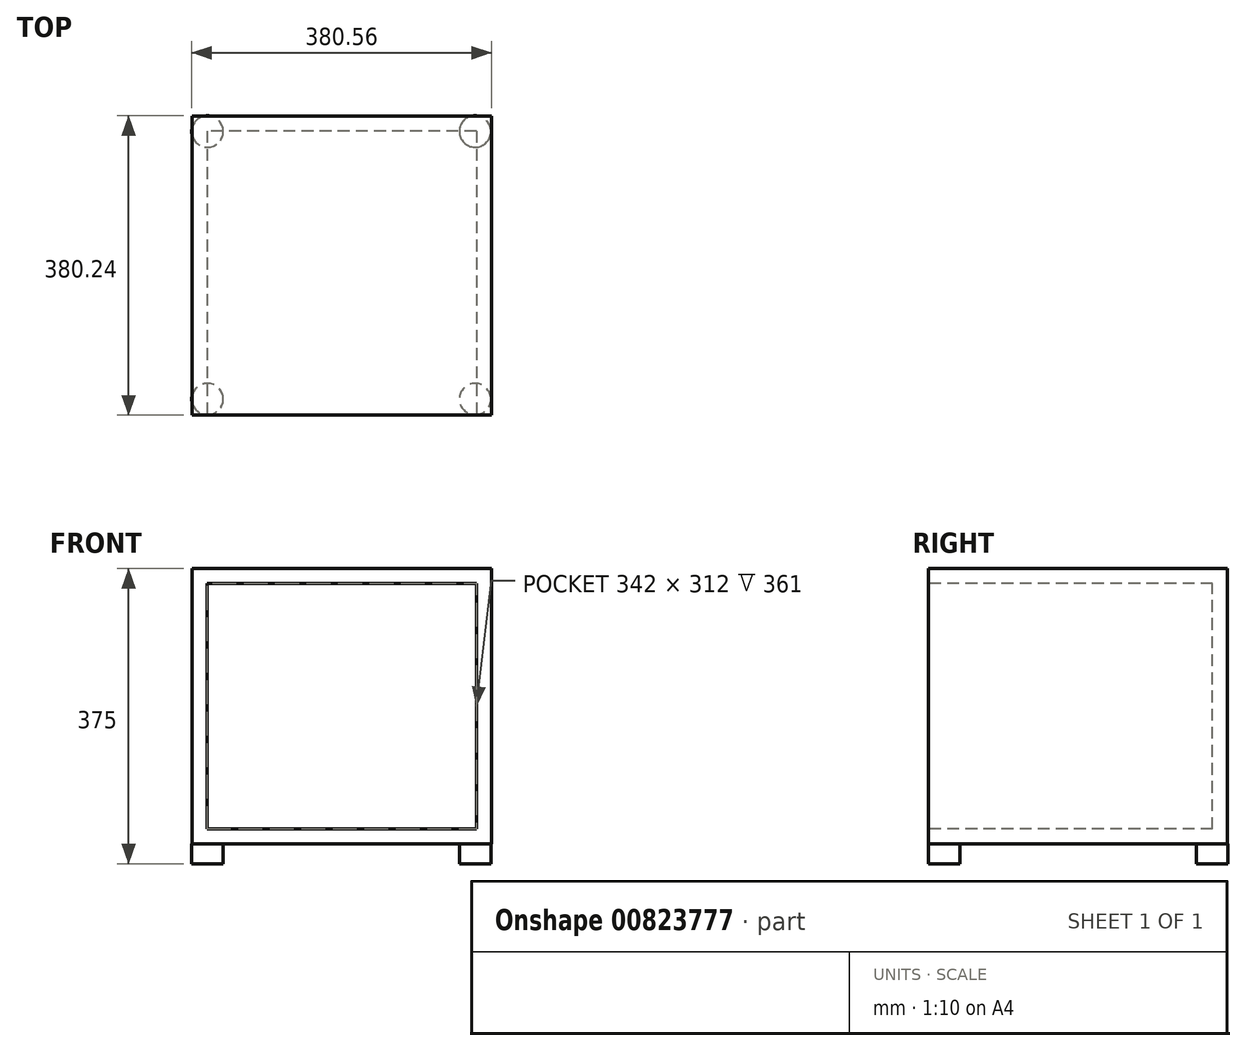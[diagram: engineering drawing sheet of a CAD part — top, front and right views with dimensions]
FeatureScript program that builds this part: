
annotation { "Feature Type Name" : "Feature", "Feature Type Description" : "" }
export const myFeature = defineFeature(function(context is Context, id is Id, definition is map)
    precondition{}
    {
        {
            var Q0;
            Q0=qCreatedBy(makeId("Top.planeOp"),FACE);
            var sketch = newSketch(context, id + "F0", { "sketchPlane" : qUnion([Q0])});
            skLineSegment(sketch, "E0.bottom", {"start": v(190, -190) * mm, "end": v(-190, -190) * mm});
            skLineSegment(sketch, "E0.top", {"start": v(190, 190) * mm, "end": v(-190, 190) * mm});
            skLineSegment(sketch, "E0.left", {"start": v(190, -190) * mm, "end": v(190, 190) * mm});
            skLineSegment(sketch, "E0.right", {"start": v(-190, -190) * mm, "end": v(-190, 190) * mm});
            skPoint(sketch, "E0.middle", {"position": v(0, 0) * mm});
            skSolve(sketch);
        }
        {
            var Q0;
            Q0=makeQuery(id+"F0.imprint","IMPRINT",FACE,{"disambiguationData":[TD([[makeQuery(id+"F0.imprint","IMPRINT",EDGE,{"derivedFrom":sQuery(id+"F0.wireOp",EDGE,"E0.bottom")}),-1.0]])]});
            extrude(context, id + "F1", {"entities" : qUnion([Q0]), "depth" : 350 * mm, "offsetDistance" : 25 * mm});
        }
        {
            var Q0;
            Q0=makeQuery(id+"F1.opExtrude","SWEPT_FACE",FACE,{"disambiguationData":[OSD([sQuery(id+"F0.wireOp",EDGE,"E0.bottom")])]});
            var sketch = newSketch(context, id + "F2", { "sketchPlane" : qUnion([Q0])});
            skLineSegment(sketch, "E1.bottom", {"start": v(171, 19) * mm, "end": v(-171, 19) * mm});
            skLineSegment(sketch, "E1.top", {"start": v(171, 331) * mm, "end": v(-171, 331) * mm});
            skLineSegment(sketch, "E1.left", {"start": v(171, 19) * mm, "end": v(171, 331) * mm});
            skLineSegment(sketch, "E1.right", {"start": v(-171, 19) * mm, "end": v(-171, 331) * mm});
            skPoint(sketch, "E1.middle", {"position": v(0, 175) * mm});
            skSolve(sketch);
        }
        {
            var Q0;
            Q0=makeQuery(id+"F2.imprint","IMPRINT",FACE,{"disambiguationData":[TD([[makeQuery(id+"F2.imprint","IMPRINT",EDGE,{"derivedFrom":sQuery(id+"F2.wireOp",EDGE,"E1.bottom")}),-1.0]])]});
            extrude(context, id + "F3", {"entities" : qUnion([Q0]), "operationType" : NewBodyOperationType.REMOVE, "oppositeDirection" : true, "depth" : 361 * mm, "offsetDistance" : 25 * mm});
        }
        {
            var Q0;
            Q0=makeQuery(id+"F0.imprint","IMPRINT",FACE,{"disambiguationData":[TD([[makeQuery(id+"F0.imprint","IMPRINT",EDGE,{"derivedFrom":sQuery(id+"F0.wireOp",EDGE,"E0.bottom")}),-1.0]])]});
            var sketch = newSketch(context, id + "F4", { "sketchPlane" : qUnion([Q0])});
            skCircle(sketch, "E2", {"center": v(169.44, -169.76) * mm, "radius": 20 * mm});
            skCircle(sketch, "E3", {"center": v(169.44, 170.24) * mm, "radius": 20 * mm});
            skCircle(sketch, "E4", {"center": v(-170.56, 170.24) * mm, "radius": 20 * mm});
            skCircle(sketch, "E5", {"center": v(-170.56, -169.76) * mm, "radius": 20 * mm});
            skSolve(sketch);
        }
        {
            var Q0;
            Q0 = qSketchRegion(id + "F4", true);
            extrude(context, id + "F5", {"entities" : qUnion([Q0]), "operationType" : NewBodyOperationType.ADD, "oppositeDirection" : true, "depth" : 25 * mm, "offsetDistance" : 25 * mm});
        }
    });
